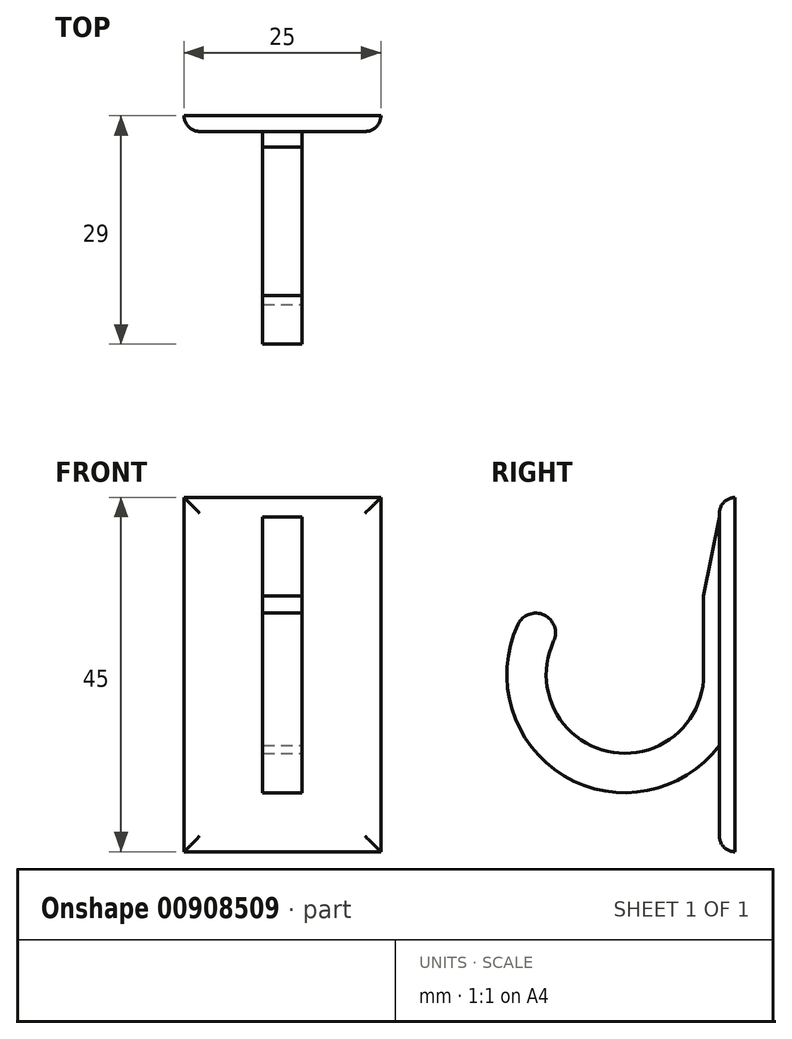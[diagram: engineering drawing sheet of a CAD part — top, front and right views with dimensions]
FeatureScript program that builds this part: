
annotation { "Feature Type Name" : "Feature", "Feature Type Description" : "" }
export const myFeature = defineFeature(function(context is Context, id is Id, definition is map)
    precondition{}
    {
        {
            var Q0;
            Q0=qCreatedBy(makeId("Front.planeOp"),FACE);
            var sketch = newSketch(context, id + "F0", { "sketchPlane" : qUnion([Q0])});
            skLineSegment(sketch, "E0.bottom", {"start": v(12.5, 22.5) * mm, "end": v(-12.5, 22.5) * mm});
            skLineSegment(sketch, "E0.top", {"start": v(12.5, -22.5) * mm, "end": v(-12.5, -22.5) * mm});
            skLineSegment(sketch, "E0.left", {"start": v(12.5, 22.5) * mm, "end": v(12.5, -22.5) * mm});
            skLineSegment(sketch, "E0.right", {"start": v(-12.5, 22.5) * mm, "end": v(-12.5, -22.5) * mm});
            skPoint(sketch, "E0.middle", {"position": v(0, 0) * mm});
            skSolve(sketch);
        }
        {
            var Q0;
            Q0 = qSketchRegion(id + "F0", true);
            extrude(context, id + "F1", {"entities" : qUnion([Q0]), "depth" : 2 * mm, "offsetDistance" : 25 * mm});
        }
        {
            var Q0;
            Q0=makeQuery(id+"F1.opExtrude","CAP_FACE",FACE,{"disambiguationData":[OSD([sQuery(id+"F0.wireOp",EDGE,"E0.bottom"),sQuery(id+"F0.wireOp",EDGE,"E0.top"),sQuery(id+"F0.wireOp",EDGE,"E0.left"),sQuery(id+"F0.wireOp",EDGE,"E0.right")])],"isStart":false});
            var sketch = newSketch(context, id + "F2", { "sketchPlane" : qUnion([Q0])});
            skLineSegment(sketch, "E1", {"start": v(0, 0) * mm, "end": v(0, 20) * mm, "construction": true});
            skLineSegment(sketch, "E2", {"start": v(0, 20) * mm, "end": v(-2.5, 20) * mm, "construction": true});
            skLineSegment(sketch, "E3", {"start": v(-2.5, 20) * mm, "end": v(-2.5, -15) * mm});
            skLineSegment(sketch, "E4", {"start": v(-2.5, -15) * mm, "end": v(2.5, -15) * mm});
            skLineSegment(sketch, "E5", {"start": v(2.5, -15) * mm, "end": v(2.5, 20) * mm});
            skLineSegment(sketch, "E6", {"start": v(2.5, 20) * mm, "end": v(-2.5, 20) * mm});
            skSolve(sketch);
        }
        {
            var Q0;
            Q0=makeQuery(id+"F2.imprint","IMPRINT",FACE,{"disambiguationData":[TD([[makeQuery(id+"F2.imprint","IMPRINT",EDGE,{"derivedFrom":sQuery(id+"F2.wireOp",EDGE,"E3")}),1.0]])]});
            extrude(context, id + "F3", {"entities" : qUnion([Q0]), "operationType" : NewBodyOperationType.ADD, "depth" : 50 * mm, "offsetDistance" : 25 * mm});
        }
        {
            var Q0;
            Q0=makeQuery(id+"F3.opExtrude","SWEPT_FACE",FACE,{"disambiguationData":[OSD([sQuery(id+"F2.wireOp",EDGE,"E5")])]});
            var sketch = newSketch(context, id + "F4", { "sketchPlane" : qUnion([Q0])});
            skLineSegment(sketch, "E7", {"start": v(-2, 20) * mm, "end": v(-4, 20) * mm, "construction": true});
            skLineSegment(sketch, "E8", {"start": v(-4, 20) * mm, "end": v(-4, 10) * mm, "construction": true});
            skLineSegment(sketch, "E9", {"start": v(-4, 10) * mm, "end": v(-4, 0) * mm, "construction": true});
            skLineSegment(sketch, "E10", {"start": v(-2, 20) * mm, "end": v(-4, 10) * mm});
            skLineSegment(sketch, "E11", {"start": v(-4, 0) * mm, "end": v(-4, 10) * mm});
            skLineSegment(sketch, "E12", {"start": v(-4, 0) * mm, "end": v(-14, 0) * mm, "construction": true});
            skArc(sketch, "E13", {"start": v(-23.8, -1.99) * mm, "mid": v(-13, -9.95) * mm, "end": v(-4, 0) * mm});
            skArc(sketch, "E14", {"start": v(-28.7, -2.98) * mm, "mid": v(-17.3, -14.63) * mm, "end": v(-2, -9) * mm});
            skLineSegment(sketch, "E15", {"start": v(-26.5, 0) * mm, "end": v(-26, 0) * mm, "construction": true});
            skPoint(sketch, "E16.orphan", {"position": v(-24, 0) * mm});
            skPoint(sketch, "E17.orphan", {"position": v(-29, 0) * mm});
            skLineSegment(sketch, "E18", {"start": v(-2, 20) * mm, "end": v(-2, -9) * mm});
            skArc(sketch, "E19", {"start": v(-27.58, 6.38) * mm, "mid": v(-21.73, -12.86) * mm, "end": v(-2, -9) * mm});
            skArc(sketch, "E20", {"start": v(-23.05, 4.25) * mm, "mid": v(-16.18, -9.76) * mm, "end": v(-4, 0) * mm});
            skArc(sketch, "E21", {"start": v(-23.05, 4.25) * mm, "mid": v(-24.25, 7.58) * mm, "end": v(-27.58, 6.38) * mm});
            skLineSegment(sketch, "E22", {"start": v(-2, 20) * mm, "end": v(-52, 20) * mm});
            skLineSegment(sketch, "E23", {"start": v(-52, 20) * mm, "end": v(-52, -15) * mm});
            skLineSegment(sketch, "E24", {"start": v(-52, -15) * mm, "end": v(-2, -15) * mm});
            skLineSegment(sketch, "E25", {"start": v(-2, -15) * mm, "end": v(-2, -9) * mm});
            skSolve(sketch);
        }
        {
            var Q0;
            Q0=makeQuery(id+"F4.imprint","IMPRINT",FACE,{"disambiguationData":[TD([[makeQuery(id+"F4.imprint","IMPRINT",EDGE,{"derivedFrom":sQuery(id+"F4.wireOp",EDGE,"E10")}),-1.0]])]});
            var Q1;
            {var subQ0=sQuery(id+"F4.wireOp",EDGE,"E25");Q1=makeQuery(id+"F4.imprint","IMPRINT",FACE,{"disambiguationData":[TD([[makeQuery(id+"F4.imprint","IMPRINT",EDGE,{"derivedFrom":subQ0}),1.0]])]});}
            extrude(context, id + "F5", {"entities" : qUnion([Q0, Q1]), "operationType" : NewBodyOperationType.REMOVE, "endBound" : BoundingType.UP_TO_NEXT, "oppositeDirection" : true, "depth" : 25 * mm, "offsetDistance" : 25 * mm});
        }
        {
            var Q0;
            Q0=makeQuery(id+"F5.boolean.opBoolean","COPY",EDGE,{"derivedFrom":makeQuery(id+"F5.opExtrude","CAP_EDGE",EDGE,{"disambiguationData":[OSD([sQuery(id+"F4.wireOp",EDGE,"E21")])],"isStart":true})});
            var Q1;
            Q1=makeQuery(id+"F5.boolean.opBoolean","COPY",EDGE,{"derivedFrom":makeQuery(id+"F5.opExtrude","CAP_EDGE",EDGE,{"disambiguationData":[OSD([sQuery(id+"F4.wireOp",EDGE,"E21")])],"isStart":false})});
            var Q2;
            Q2=makeQuery(id+"F1.opExtrude","CAP_EDGE",EDGE,{"disambiguationData":[OSD([sQuery(id+"F0.wireOp",EDGE,"E0.bottom")])],"isStart":false});
            var Q3;
            Q3=makeQuery(id+"F1.opExtrude","CAP_EDGE",EDGE,{"disambiguationData":[OSD([sQuery(id+"F0.wireOp",EDGE,"E0.right")])],"isStart":false});
            var Q4;
            Q4=makeQuery(id+"F1.opExtrude","CAP_EDGE",EDGE,{"disambiguationData":[OSD([sQuery(id+"F0.wireOp",EDGE,"E0.top")])],"isStart":false});
            var Q5;
            Q5=makeQuery(id+"F1.opExtrude","CAP_EDGE",EDGE,{"disambiguationData":[OSD([sQuery(id+"F0.wireOp",EDGE,"E0.left")])],"isStart":false});
            fillet(context, id + "F6", {"entities" : qUnion([Q0, Q1, Q2, Q3, Q4, Q5]), "radius" : 2 * mm, "tangentPropagation" : true, "allowEdgeOverflow" : false});
        }
    });
